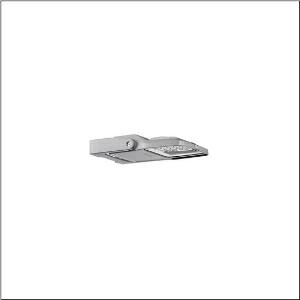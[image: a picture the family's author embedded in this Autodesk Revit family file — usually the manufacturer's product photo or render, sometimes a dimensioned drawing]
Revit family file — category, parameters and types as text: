
# Revit family: floodlight_fl_21_iq_micro___pl64_5xa7761a4e2a_05f9
name_source: partatom
category: Lighting Fixtures
units: mm (PartAtom-declared; Revit-internal decimal feet)

## family parameters
Cut with Voids When Loaded = No
Host = Face
Light Source = No
Part Type = Normal
Room Calculation Point = No
Round Connector Dimension = Use Diameter
Shared = No

## types (1)
- --- (1 x LED, 2980 lm, 23.1 W, 4000K)
    Apparent Load = 23 VA
    CIE Flux Codes = 28 80 98 100 100
    Color Rendering = 70
    Color Temperature = 4000K
    Default Elevation = 1800 mm
    Description = Floodlight FL 21 iQ micro, floodlight, primary light control with lens, of PMMA, primary optical cover: protective disc, of toughened safety glass, transparent, light distribution: PL64, light emission: direct distribution, installation type: surface-mounted, LED, High Power LED, rated luminous flux: 2.980lm, luminous efficacy: 129lm/W, light colour: 740, colour temperature: 4000K, control: optimised constant luminous flux control (CLO 2.0), Desk-Remote (wireless, voltage-free reading and setting of iQ features in the workshop via application-optimized NFC function/RFID function), Light-Fading, Smart-Wire, Night-Set, Lumen-Switch, Temp-Guard, Auto-Match, with terminal, 6-pole, mains connection: 220..240V, AC, 50/60Hz, start of lifetime: 23W, end of service life: 24W, reduction: 11W, luminaire housing, of diecast aluminium, powder-coated, Siteco® metallic grey (DB 702S), corrosivity category C5 mid according to DIN EN ISO 12944, sealing non-destructively replaceable, design bracket, of diecast aluminium, powder-coated, Siteco® metallic grey (DB 702S), protection rating (complete): IP66, insulation class (complete): insulation class II (safety insulation), certification: CE, ENEC, VDE, protection symbol: D, impact resistance: IK07, permissible operating ambient temperature: -40..+40°C, permissible operating ambient temperature for outdoor applications: -40..+50°C, standard: DIN EN 12944, LABS conformity tested according to VDMA 24364:2018-05, packaging unit: 1 piece

Light Distribution: PL64
    Height = 65 mm
    Lamp = 1 x LED
    Lamp Light Flux = 2980 lm
    Lamp Power = 23.1 W
    Lamp count = 1
    Length = 312 mm
    Luminous efficacy = 129 lm/W
    Manufacturer = Siteco
    ModVariant = No
    Model = 5XA7761A4E2A
    Mounting Place = Wall
    Mounting Type = Surface mounted
    Number of Poles = 1
    OnlyDefault = Yes
    Power Factor = 1
    Product Name = Floodlight FL 21 iQ micro | PL64
    Product group = floodlight | wall mounted
    ProductGroupID = 2001
    Protection Class = Protection class II
    Protection Degree = IP 66
    RLX_Detail_Level = 1
    RLX_Emergency_Light_Flux = 0 lm
    RLX_Emergency_Type = 0
    RLX_Emergency_Type_DB = No
    RlxData = <blob elided: 97469 chars, md5=0c19a45b>
    Socket = socket
    Standby Power = 0 W
    System Light Flux = 2980 lm
    System Power = 23 W
    Type Comments = factory setting: luminous flux: 100 % | dim-lin: 254 | 455 mA
    Type Image = l_1006878.jpg
    URL = http://relux.com
    VarID = @adj_152295
    Voltage = 0 V
    Weight = 0.00 kg
    Width = 230 mm

## geometry (parser evidence)
native form markers: Blend x4, Sweep x14
no freeform markers — native parametric forms only
